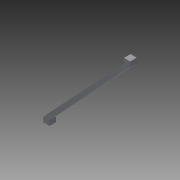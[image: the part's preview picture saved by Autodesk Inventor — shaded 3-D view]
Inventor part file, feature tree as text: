
AUTODESK INVENTOR PART (.ipt)
format: ipt  version: 2013 (Build 170138000, 138)  size: 74,240 bytes
history: native  units: in
note: dims shown in document units (in); Inventor stores cm internally (conversion verified against a paired STEP export)
features: extrude x1, sketch x1
ambient origin geometry x8: Origin, YZ Plane, XZ Plane, XY Plane, X Axis, Y Axis, Z Axis, Center Point
bodies: Solid1 (feature_tree)
feature tree (2):
  extrude  "Extrusion1"  Depth=0.3in
  sketch  "Sketch1"  dims[d0=0.375in d1=0.3in d2=0.3in d3=0.375in d4=4.534in d5=5.25in d6=0.3in d7=0.4in d8=0.0in]
